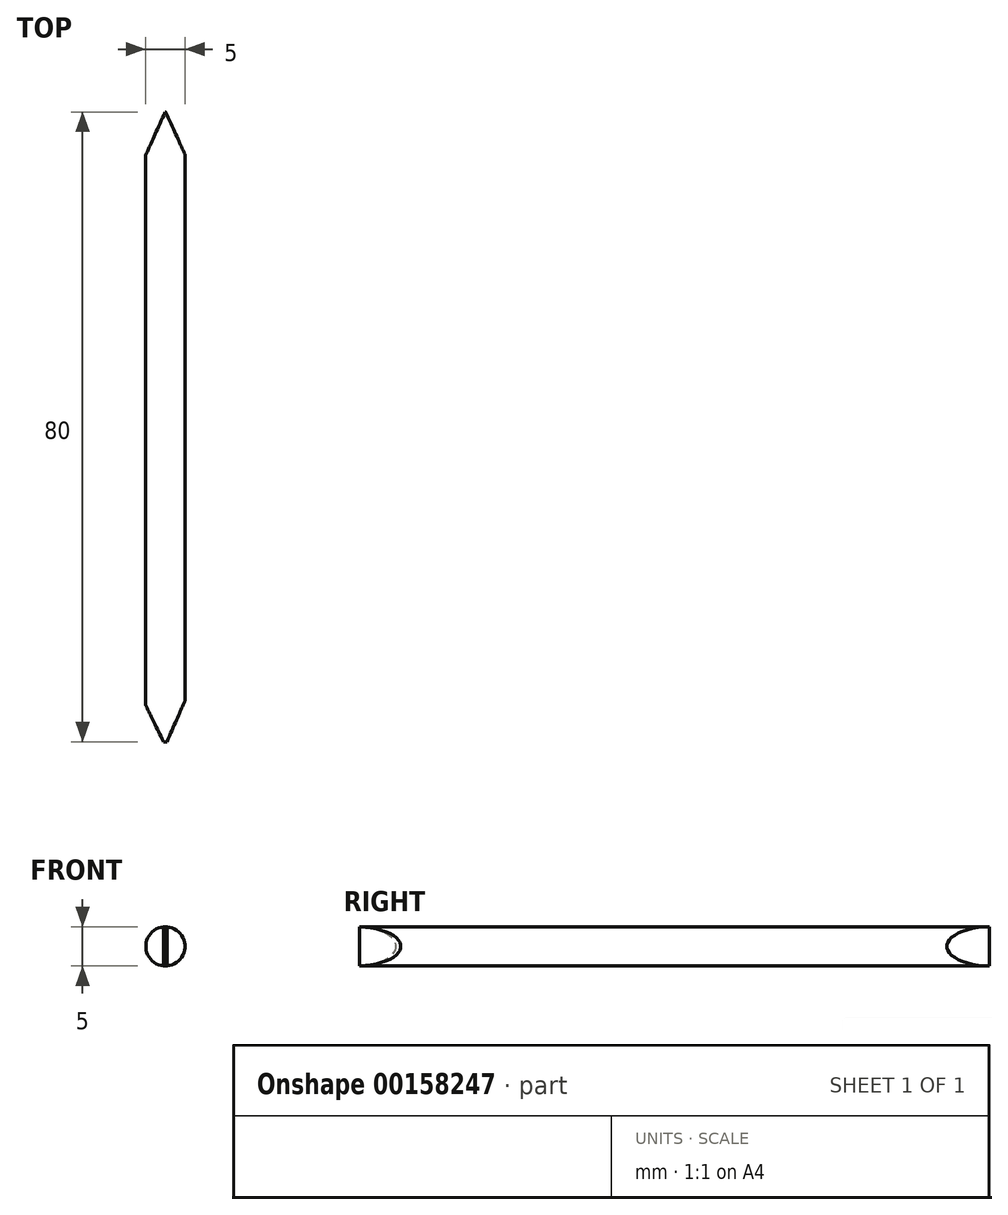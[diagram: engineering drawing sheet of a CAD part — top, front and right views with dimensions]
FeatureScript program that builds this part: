
annotation { "Feature Type Name" : "Feature", "Feature Type Description" : "" }
export const myFeature = defineFeature(function(context is Context, id is Id, definition is map)
    precondition{}
    {
        {
            var Q0;
            Q0=qCreatedBy(makeId("Front.planeOp"),FACE);
            var sketch = newSketch(context, id + "F0", { "sketchPlane" : qUnion([Q0])});
            skCircle(sketch, "E0", {"center": v(0, 0) * mm, "radius": 2.5 * mm});
            skSolve(sketch);
        }
        {
            var Q0;
            Q0=makeQuery(id+"F0.imprint","IMPRINT",FACE,{"disambiguationData":[TD([[makeQuery(id+"F0.imprint","IMPRINT",EDGE,{"derivedFrom":sQuery(id+"F0.wireOp",EDGE,"E0")}),1.0]])]});
            extrude(context, id + "F1", {"entities" : qUnion([Q0]), "depth" : 80 * mm, "symmetric" : true});
        }
        {
            var Q0;
            Q0=qCreatedBy(makeId("Top.planeOp"),FACE);
            var sketch = newSketch(context, id + "F2", { "sketchPlane" : qUnion([Q0])});
            skLineSegment(sketch, "E1", {"start": v(-3.14, 33.13) * mm, "end": v(0, 40.06) * mm});
            skLineSegment(sketch, "E2", {"start": v(0, 40.06) * mm, "end": v(3.16, 33.13) * mm});
            skLineSegment(sketch, "E3", {"start": v(-3.14, 33.13) * mm, "end": v(-3.14, 40.85) * mm});
            skLineSegment(sketch, "E4", {"start": v(-3.14, 40.85) * mm, "end": v(3.4, 40.85) * mm});
            skLineSegment(sketch, "E5", {"start": v(3.4, 40.85) * mm, "end": v(3.16, 33.13) * mm});
            skSolve(sketch);
        }
        {
            var Q0;
            Q0=qCreatedBy(makeId("Top.planeOp"),FACE);
            var sketch = newSketch(context, id + "F3", { "sketchPlane" : qUnion([Q0])});
            skLineSegment(sketch, "E6", {"start": v(-4.27, -31.72) * mm, "end": v(0, -40.49) * mm});
            skLineSegment(sketch, "E7", {"start": v(0, -40.49) * mm, "end": v(4.05, -31.2) * mm});
            skLineSegment(sketch, "E8", {"start": v(4.05, -31.2) * mm, "end": v(5.26, -31.72) * mm});
            skLineSegment(sketch, "E9", {"start": v(5.26, -31.72) * mm, "end": v(5.02, -41.2) * mm});
            skLineSegment(sketch, "E10", {"start": v(5.02, -41.2) * mm, "end": v(-4.53, -41.37) * mm});
            skLineSegment(sketch, "E11", {"start": v(-4.53, -41.37) * mm, "end": v(-4.27, -31.72) * mm});
            skSolve(sketch);
        }
        {
            var Q0;
            Q0=makeQuery(id+"F3.imprint","IMPRINT",FACE,{"disambiguationData":[TD([[makeQuery(id+"F3.imprint","IMPRINT",EDGE,{"derivedFrom":sQuery(id+"F3.wireOp",EDGE,"E6")}),-1.0]])]});
            extrude(context, id + "F4", {"entities" : qUnion([Q0]), "operationType" : NewBodyOperationType.REMOVE, "depth" : 25 * mm, "symmetric" : true});
        }
        {
            var Q0;
            Q0=makeQuery(id+"F2.imprint","IMPRINT",FACE,{"disambiguationData":[TD([[makeQuery(id+"F2.imprint","IMPRINT",EDGE,{"derivedFrom":sQuery(id+"F2.wireOp",EDGE,"E1")}),1.0]])]});
            extrude(context, id + "F5", {"entities" : qUnion([Q0]), "operationType" : NewBodyOperationType.REMOVE, "oppositeDirection" : true, "depth" : 25 * mm, "symmetric" : true});
        }
    });
